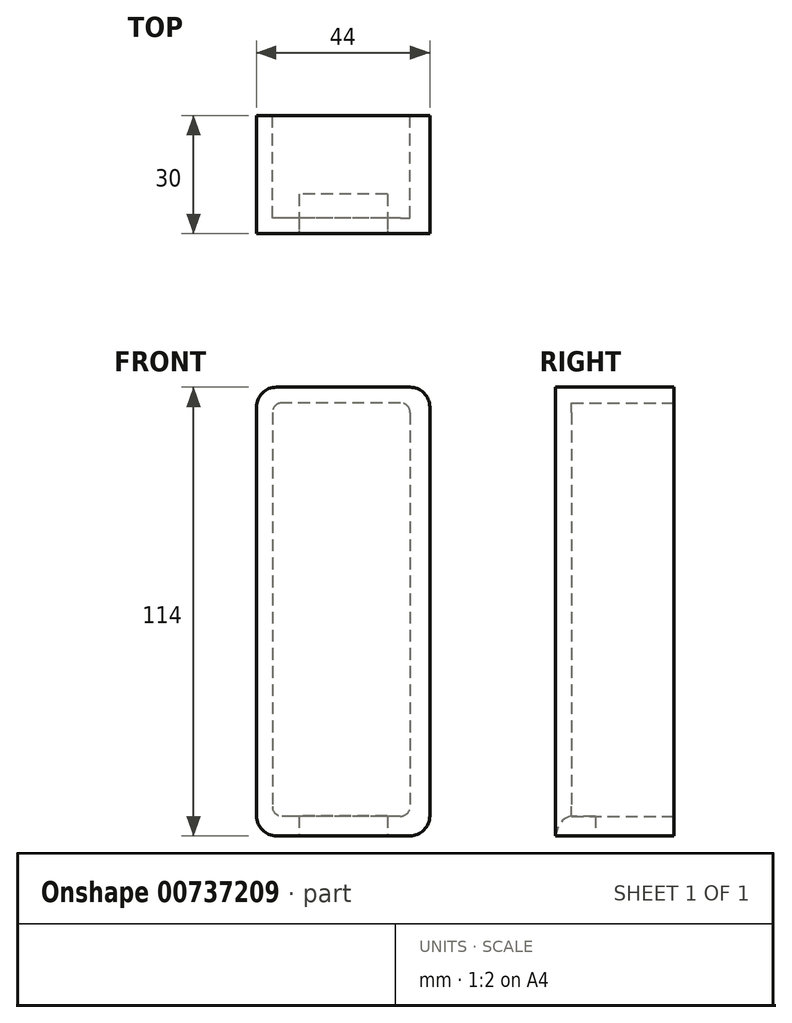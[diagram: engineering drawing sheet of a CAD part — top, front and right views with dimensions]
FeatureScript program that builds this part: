
annotation { "Feature Type Name" : "Feature", "Feature Type Description" : "" }
export const myFeature = defineFeature(function(context is Context, id is Id, definition is map)
    precondition{}
    {
        {
            var Q0;
            Q0=qCreatedBy(makeId("Top.planeOp"),FACE);
            var sketch = newSketch(context, id + "F0", { "sketchPlane" : qUnion([Q0])});
            skLineSegment(sketch, "E0.bottom", {"start": v(-22, 15) * mm, "end": v(22, 15) * mm});
            skLineSegment(sketch, "E0.top", {"start": v(-22, -15) * mm, "end": v(22, -15) * mm});
            skLineSegment(sketch, "E0.left", {"start": v(-22, 15) * mm, "end": v(-22, -15) * mm});
            skLineSegment(sketch, "E0.right", {"start": v(22, 15) * mm, "end": v(22, -15) * mm});
            skPoint(sketch, "E0.middle", {"position": v(0, 0) * mm});
            skSolve(sketch);
        }
        {
            var Q0;
            Q0=makeQuery(id+"F0.imprint","IMPRINT",FACE,{"disambiguationData":[TD([[makeQuery(id+"F0.imprint","IMPRINT",EDGE,{"derivedFrom":sQuery(id+"F0.wireOp",EDGE,"E0.bottom")}),-1.0]])]});
            extrude(context, id + "F1", {"entities" : qUnion([Q0]), "depth" : 114 * mm, "offsetDistance" : 25.4 * mm});
        }
        {
            var Q0;
            Q0=makeQuery(id+"F1.opExtrude","SWEPT_FACE",FACE,{"disambiguationData":[OSD([sQuery(id+"F0.wireOp",EDGE,"E0.bottom")])]});
            var sketch = newSketch(context, id + "F2", { "sketchPlane" : qUnion([Q0])});
            skLineSegment(sketch, "E1.bottom", {"start": v(-17, 110) * mm, "end": v(18, 110) * mm});
            skLineSegment(sketch, "E1.top", {"start": v(-17, 5) * mm, "end": v(18, 5) * mm});
            skLineSegment(sketch, "E1.left", {"start": v(-17, 110) * mm, "end": v(-17, 5) * mm});
            skLineSegment(sketch, "E1.right", {"start": v(18, 110) * mm, "end": v(18, 5) * mm});
            skPoint(sketch, "E1.middle", {"position": v(0.5, 57.5) * mm});
            skSolve(sketch);
        }
        {
            var Q0;
            Q0=makeQuery(id+"F2.imprint","IMPRINT",FACE,{"disambiguationData":[TD([[makeQuery(id+"F2.imprint","IMPRINT",EDGE,{"derivedFrom":sQuery(id+"F2.wireOp",EDGE,"E1.bottom")}),-1.0]])]});
            extrude(context, id + "F3", {"entities" : qUnion([Q0]), "operationType" : NewBodyOperationType.REMOVE, "oppositeDirection" : true, "depth" : 26 * mm, "offsetDistance" : 25.4 * mm});
        }
        {
            var Q0;
            Q0=makeQuery(id+"F1.opExtrude","CAP_EDGE",EDGE,{"disambiguationData":[OSD([sQuery(id+"F0.wireOp",EDGE,"E0.right")])],"isStart":true});
            var Q1;
            Q1=makeQuery(id+"F1.opExtrude","CAP_EDGE",EDGE,{"disambiguationData":[OSD([sQuery(id+"F0.wireOp",EDGE,"E0.left")])],"isStart":true});
            var Q2;
            Q2=makeQuery(id+"F1.opExtrude","CAP_EDGE",EDGE,{"disambiguationData":[OSD([sQuery(id+"F0.wireOp",EDGE,"E0.left")])],"isStart":false});
            var Q3;
            Q3=makeQuery(id+"F1.opExtrude","CAP_EDGE",EDGE,{"disambiguationData":[OSD([sQuery(id+"F0.wireOp",EDGE,"E0.right")])],"isStart":false});
            fillet(context, id + "F4", {"entities" : qUnion([Q0, Q1, Q2, Q3]), "radius" : 5.08 * mm, "tangentPropagation" : true, "allowEdgeOverflow" : false});
        }
        {
            var Q0;
            Q0=makeQuery(id+"F3.boolean.opBoolean","COPY",EDGE,{"derivedFrom":makeQuery(id+"F3.opExtrude","SWEPT_EDGE",EDGE,{"disambiguationData":[OSD([sQuery(id+"F2.wireOp",EDGE,"E1.bottom"),sQuery(id+"F2.wireOp",EDGE,"E1.left")])]})});
            var Q1;
            Q1=makeQuery(id+"F3.boolean.opBoolean","COPY",EDGE,{"derivedFrom":makeQuery(id+"F3.opExtrude","SWEPT_EDGE",EDGE,{"disambiguationData":[OSD([sQuery(id+"F2.wireOp",EDGE,"E1.bottom"),sQuery(id+"F2.wireOp",EDGE,"E1.right")])]})});
            var Q2;
            Q2=makeQuery(id+"F3.boolean.opBoolean","COPY",EDGE,{"derivedFrom":makeQuery(id+"F3.opExtrude","SWEPT_EDGE",EDGE,{"disambiguationData":[OSD([sQuery(id+"F2.wireOp",EDGE,"E1.top"),sQuery(id+"F2.wireOp",EDGE,"E1.left")])]})});
            var Q3;
            Q3=makeQuery(id+"F3.boolean.opBoolean","COPY",EDGE,{"derivedFrom":makeQuery(id+"F3.opExtrude","SWEPT_EDGE",EDGE,{"disambiguationData":[OSD([sQuery(id+"F2.wireOp",EDGE,"E1.top"),sQuery(id+"F2.wireOp",EDGE,"E1.right")])]})});
            fillet(context, id + "F5", {"entities" : qUnion([Q0, Q1, Q2, Q3]), "radius" : 2.45 * mm, "tangentPropagation" : true, "allowEdgeOverflow" : false});
        }
        {
            var Q0;
            Q0=makeQuery(id+"F1.opExtrude","CAP_FACE",FACE,{"disambiguationData":[OSD([sQuery(id+"F0.wireOp",EDGE,"E0.bottom"),sQuery(id+"F0.wireOp",EDGE,"E0.top"),sQuery(id+"F0.wireOp",EDGE,"E0.left"),sQuery(id+"F0.wireOp",EDGE,"E0.right")])],"isStart":true});
            var sketch = newSketch(context, id + "F6", { "sketchPlane" : qUnion([Q0])});
            skLineSegment(sketch, "E2.bottom", {"start": v(11.23, 4.96) * mm, "end": v(-11.23, 4.96) * mm});
            skLineSegment(sketch, "E2.top", {"start": v(11.23, 14.9) * mm, "end": v(-11.23, 14.9) * mm});
            skLineSegment(sketch, "E2.left", {"start": v(11.23, 4.96) * mm, "end": v(11.23, 14.9) * mm});
            skLineSegment(sketch, "E2.right", {"start": v(-11.23, 4.96) * mm, "end": v(-11.23, 14.9) * mm});
            skPoint(sketch, "E2.middle", {"position": v(0, 9.93) * mm});
            skSolve(sketch);
        }
        {
            var Q0;
            Q0=makeQuery(id+"F6.imprint","IMPRINT",FACE,{"disambiguationData":[TD([[makeQuery(id+"F6.imprint","IMPRINT",EDGE,{"derivedFrom":sQuery(id+"F6.wireOp",EDGE,"E2.bottom")}),-1.0]])]});
            extrude(context, id + "F7", {"entities" : qUnion([Q0]), "operationType" : NewBodyOperationType.REMOVE, "oppositeDirection" : true, "depth" : 5.08 * mm, "offsetDistance" : 25.4 * mm});
        }
        {
            var Q0;
            Q0=makeQuery(id+"F7.boolean.opBoolean","COPY",EDGE,{"derivedFrom":makeQuery(id+"F7.opExtrude","CAP_EDGE",EDGE,{"disambiguationData":[OSD([sQuery(id+"F6.wireOp",EDGE,"E2.top")])],"isStart":false})});
            fillet(context, id + "F8", {"entities" : qUnion([Q0]), "radius" : 5.08 * mm, "tangentPropagation" : true, "allowEdgeOverflow" : false});
        }
    });
